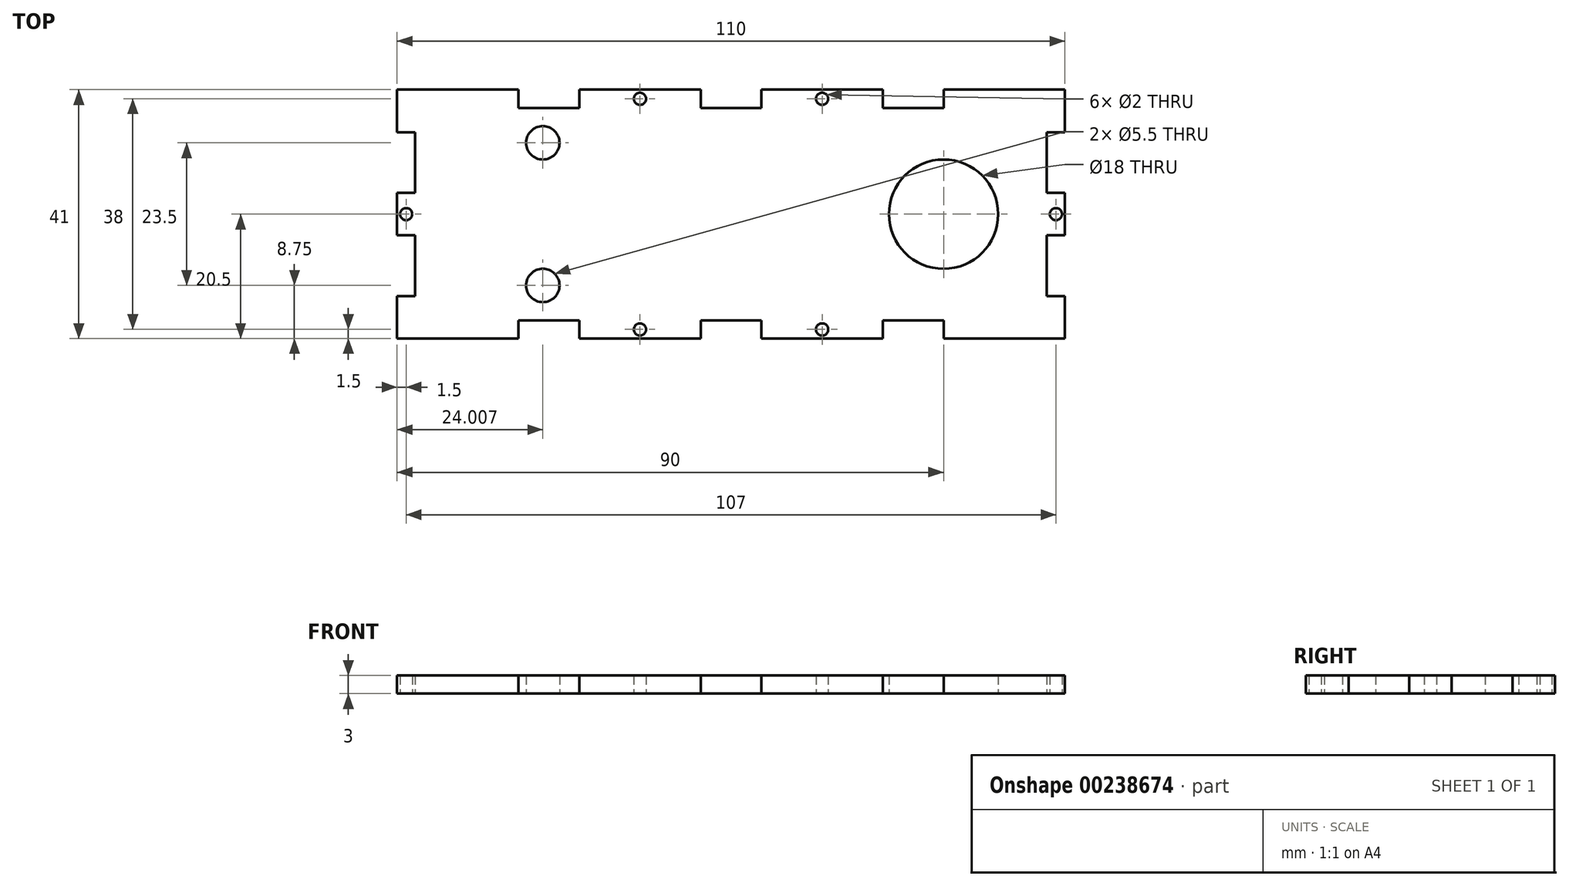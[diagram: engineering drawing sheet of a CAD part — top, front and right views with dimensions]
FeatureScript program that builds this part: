
annotation { "Feature Type Name" : "Feature", "Feature Type Description" : "" }
export const myFeature = defineFeature(function(context is Context, id is Id, definition is map)
    precondition{}
    {
        {
            var Q0;
            Q0=qCreatedBy(makeId("Top.planeOp"),FACE);
            var sketch = newSketch(context, id + "F0", { "sketchPlane" : qUnion([Q0])});
            skLineSegment(sketch, "E0", {"start": v(0, 0) * mm, "end": v(0, 7) * mm});
            skLineSegment(sketch, "E1", {"start": v(0, 7) * mm, "end": v(3, 7) * mm});
            skLineSegment(sketch, "E2", {"start": v(3, 7) * mm, "end": v(3, 17) * mm});
            skLineSegment(sketch, "E3", {"start": v(3, 17) * mm, "end": v(0, 17) * mm});
            skLineSegment(sketch, "E4", {"start": v(0, 17) * mm, "end": v(0, 24) * mm});
            skLineSegment(sketch, "E5", {"start": v(0, 24) * mm, "end": v(3, 24) * mm});
            skLineSegment(sketch, "E6", {"start": v(3, 24) * mm, "end": v(3, 34) * mm});
            skLineSegment(sketch, "E7", {"start": v(3, 34) * mm, "end": v(0, 34) * mm});
            skLineSegment(sketch, "E8", {"start": v(0, 34) * mm, "end": v(0, 41) * mm});
            skLineSegment(sketch, "E9", {"start": v(0, 41) * mm, "end": v(20, 41) * mm});
            skLineSegment(sketch, "E10", {"start": v(20, 41) * mm, "end": v(20, 38) * mm});
            skLineSegment(sketch, "E11", {"start": v(20, 38) * mm, "end": v(30, 38) * mm});
            skLineSegment(sketch, "E12", {"start": v(30, 38) * mm, "end": v(30, 41) * mm});
            skLineSegment(sketch, "E13", {"start": v(30, 41) * mm, "end": v(50, 41) * mm});
            skLineSegment(sketch, "E14", {"start": v(50, 38) * mm, "end": v(55, 38) * mm});
            skLineSegment(sketch, "E15", {"start": v(50, 41) * mm, "end": v(50, 38) * mm});
            skLineSegment(sketch, "E16", {"start": v(55, 40.92) * mm, "end": v(55, 0) * mm, "construction": true});
            skLineSegment(sketch, "E17", {"start": v(0, 20.5) * mm, "end": v(55, 20.5) * mm, "construction": true});
            skCircle(sketch, "E18", {"center": v(40, 39.5) * mm, "radius": 1 * mm});
            skPoint(sketch, "E18.centerSnap0", {"position": v(40, 41) * mm});
            skPoint(sketch, "E18.centerSnap1", {"position": v(50, 39.5) * mm});
            skCircle(sketch, "E19", {"center": v(1.5, 20.5) * mm, "radius": 1 * mm});
            skPoint(sketch, "E19.centerSnap0", {"position": v(1.5, 24) * mm});
            skLineSegment(sketch, "E20.MirrorCS", {"start": v(20, 0) * mm, "end": v(20, 3) * mm});
            skLineSegment(sketch, "E21.MirrorCS", {"start": v(50, 0) * mm, "end": v(50, 3) * mm});
            skLineSegment(sketch, "E22.MirrorCS", {"start": v(30, 3) * mm, "end": v(30, 0) * mm});
            skCircle(sketch, "E23.MirrorC", {"center": v(40, 1.5) * mm, "radius": 1 * mm});
            skLineSegment(sketch, "E24.MirrorCS", {"start": v(20, 3) * mm, "end": v(30, 3) * mm});
            skLineSegment(sketch, "E25.MirrorCS", {"start": v(30, 0) * mm, "end": v(50, 0) * mm});
            skPoint(sketch, "E26.MirrorP", {"position": v(40, 0) * mm});
            skPoint(sketch, "E27.MirrorP", {"position": v(50, 1.5) * mm});
            skLineSegment(sketch, "E28.MirrorCS", {"start": v(0, 0) * mm, "end": v(20, 0) * mm});
            skLineSegment(sketch, "E29.MirrorCS", {"start": v(50, 3) * mm, "end": v(55, 3) * mm});
            skLineSegment(sketch, "E30.MirrorCS", {"start": v(60, 41) * mm, "end": v(60, 38) * mm});
            skLineSegment(sketch, "E31.MirrorCS", {"start": v(107, 34) * mm, "end": v(110, 34) * mm});
            skLineSegment(sketch, "E32.MirrorCS", {"start": v(110, 24) * mm, "end": v(107, 24) * mm});
            skLineSegment(sketch, "E33.MirrorCS", {"start": v(110, 7) * mm, "end": v(107, 7) * mm});
            skLineSegment(sketch, "E34.MirrorCS", {"start": v(107, 17) * mm, "end": v(110, 17) * mm});
            skLineSegment(sketch, "E35.MirrorCS", {"start": v(90, 41) * mm, "end": v(90, 38) * mm});
            skLineSegment(sketch, "E36.MirrorCS", {"start": v(80, 38) * mm, "end": v(80, 41) * mm});
            skLineSegment(sketch, "E37.MirrorCS", {"start": v(60, 0) * mm, "end": v(60, 3) * mm});
            skCircle(sketch, "E38.MirrorC", {"center": v(108.5, 20.5) * mm, "radius": 1 * mm});
            skCircle(sketch, "E39.MirrorC", {"center": v(70, 1.5) * mm, "radius": 1 * mm});
            skCircle(sketch, "E40.MirrorC", {"center": v(70, 39.5) * mm, "radius": 1 * mm});
            skLineSegment(sketch, "E41.MirrorCS", {"start": v(110, 17) * mm, "end": v(110, 24) * mm});
            skLineSegment(sketch, "E42.MirrorCS", {"start": v(80, 41) * mm, "end": v(60, 41) * mm});
            skPoint(sketch, "E43.MirrorP", {"position": v(108.5, 24) * mm});
            skLineSegment(sketch, "E44.MirrorCS", {"start": v(90, 3) * mm, "end": v(80, 3) * mm});
            skLineSegment(sketch, "E45.MirrorCS", {"start": v(110, 0) * mm, "end": v(90, 0) * mm});
            skPoint(sketch, "E46.MirrorP", {"position": v(70, 41) * mm});
            skLineSegment(sketch, "E47.MirrorCS", {"start": v(107, 24) * mm, "end": v(107, 34) * mm});
            skPoint(sketch, "E48.MirrorP", {"position": v(60, 39.5) * mm});
            skLineSegment(sketch, "E49.MirrorCS", {"start": v(110, 0) * mm, "end": v(110, 7) * mm});
            skPoint(sketch, "E50.MirrorP", {"position": v(70, 0) * mm});
            skLineSegment(sketch, "E51.MirrorCS", {"start": v(110, 34) * mm, "end": v(110, 41) * mm});
            skLineSegment(sketch, "E52.MirrorCS", {"start": v(107, 7) * mm, "end": v(107, 17) * mm});
            skLineSegment(sketch, "E53.MirrorCS", {"start": v(110, 41) * mm, "end": v(90, 41) * mm});
            skLineSegment(sketch, "E54.MirrorCS", {"start": v(90, 38) * mm, "end": v(80, 38) * mm});
            skLineSegment(sketch, "E55.MirrorCS", {"start": v(80, 0) * mm, "end": v(60, 0) * mm});
            skLineSegment(sketch, "E56.MirrorCS", {"start": v(80, 3) * mm, "end": v(80, 0) * mm});
            skLineSegment(sketch, "E57.MirrorCS", {"start": v(90, 0) * mm, "end": v(90, 3) * mm});
            skPoint(sketch, "E58.MirrorP", {"position": v(60, 1.5) * mm});
            skLineSegment(sketch, "E59.MirrorCS", {"start": v(60, 3) * mm, "end": v(55, 3) * mm});
            skLineSegment(sketch, "E60.MirrorCS", {"start": v(60, 38) * mm, "end": v(55, 38) * mm});
            skCircle(sketch, "E61", {"center": v(90, 20.5) * mm, "radius": 9 * mm});
            skPoint(sketch, "E61.centerSnap0", {"position": v(110, 20.5) * mm});
            skPoint(sketch, "E62.centerSnap0", {"position": v(3, 29) * mm});
            skPoint(sketch, "E62.centerSnap1", {"position": v(25, 38) * mm});
            skPoint(sketch, "E63.centerSnap0", {"position": v(3, 12) * mm});
            skPoint(sketch, "E63.centerSnap1", {"position": v(25, 3) * mm});
            skCircle(sketch, "E64", {"center": v(24, 8.75) * mm, "radius": 2.75 * mm});
            skCircle(sketch, "E65.MirrorC", {"center": v(24, 32.25) * mm, "radius": 2.75 * mm});
            skSolve(sketch);
        }
        {
            var Q0;
            Q0=qSketchRegion(id+"F0",true);
            extrude(context, id + "F1", {"entities" : qUnion([Q0]), "depth" : 3 * mm});
        }
    });
